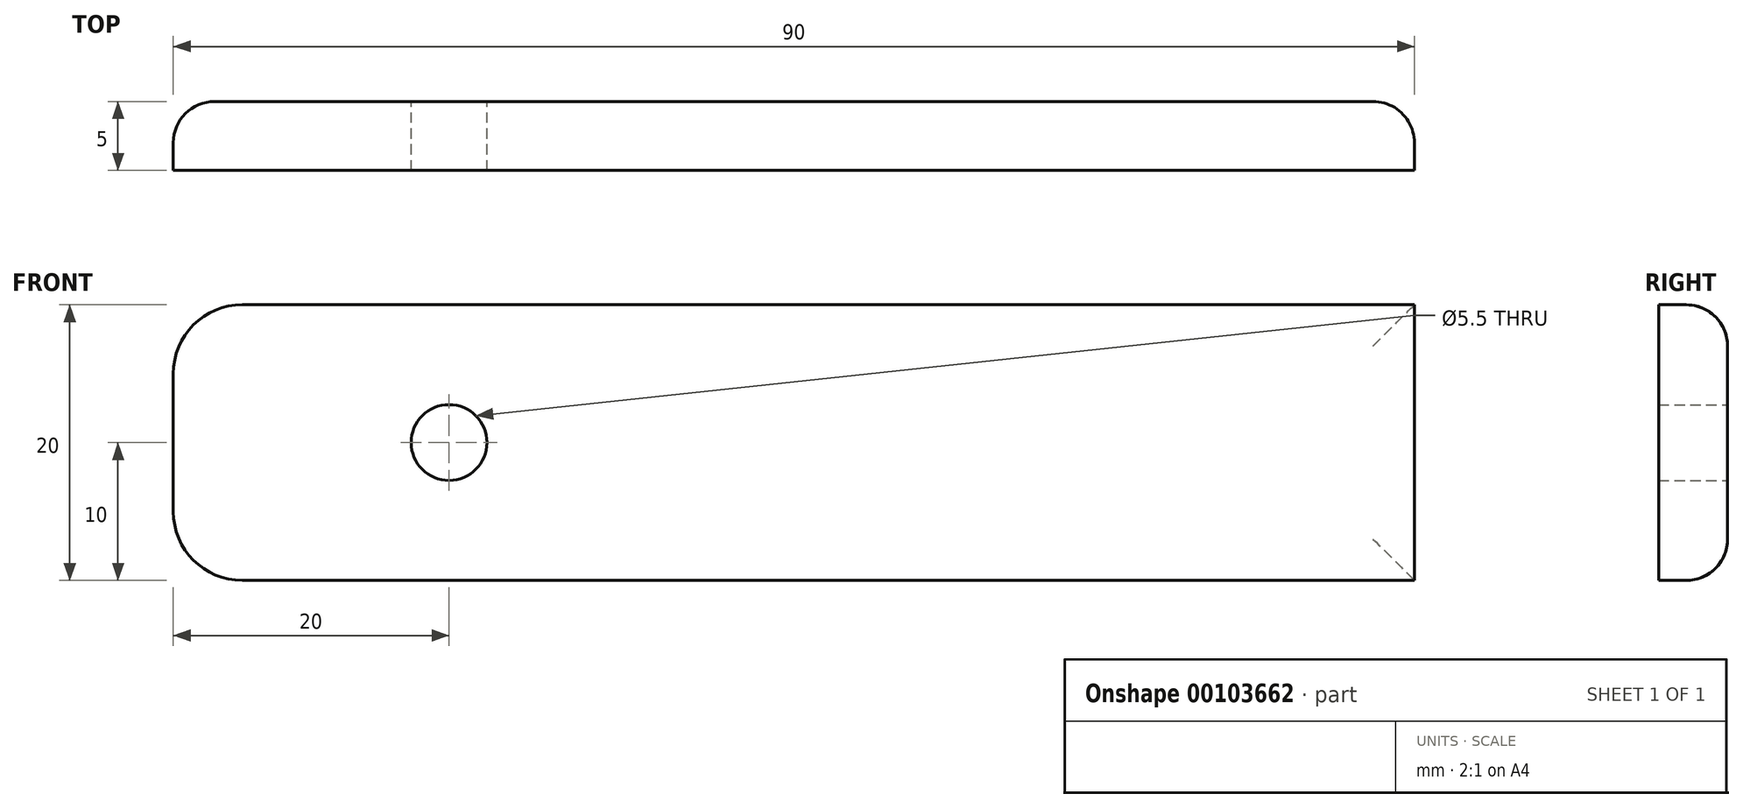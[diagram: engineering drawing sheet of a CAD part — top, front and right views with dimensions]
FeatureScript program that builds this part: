
annotation { "Feature Type Name" : "Feature", "Feature Type Description" : "" }
export const myFeature = defineFeature(function(context is Context, id is Id, definition is map)
    precondition{}
    {
        {
            var Q0;
            Q0=qCreatedBy(makeId("Top.planeOp"),FACE);
            var sketch = newSketch(context, id + "F0", { "sketchPlane" : qUnion([Q0])});
            skLineSegment(sketch, "E0.bottom", {"start": v(45, 2.5) * mm, "end": v(-45, 2.5) * mm});
            skLineSegment(sketch, "E0.top", {"start": v(45, -2.5) * mm, "end": v(-45, -2.5) * mm});
            skLineSegment(sketch, "E0.left", {"start": v(45, 2.5) * mm, "end": v(45, -2.5) * mm});
            skLineSegment(sketch, "E0.right", {"start": v(-45, 2.5) * mm, "end": v(-45, -2.5) * mm});
            skPoint(sketch, "E0.middle", {"position": v(0, 0) * mm});
            skLineSegment(sketch, "E1.left", {"start": v(45, -2.5) * mm, "end": v(45, 2.5) * mm});
            skLineSegment(sketch, "E2", {"start": v(45, -2.5) * mm, "end": v(59.13, 8.2) * mm});
            skLineSegment(sketch, "E3", {"start": v(45, 2.5) * mm, "end": v(56.96, 11.55) * mm});
            skLineSegment(sketch, "E4", {"start": v(56.96, 11.55) * mm, "end": v(59.13, 8.2) * mm});
            skSolve(sketch);
        }
        {
            var Q0;
            Q0=makeQuery(id+"F0.imprint","IMPRINT",FACE,{"disambiguationData":[TD([[makeQuery(id+"F0.imprint","IMPRINT",EDGE,{"derivedFrom":sQuery(id+"F0.wireOp",EDGE,"E0.bottom")}),1.0]])]});
            var Q1;
            Q1=makeQuery(id+"F0.imprint","IMPRINT",FACE,{"disambiguationData":[TD([[makeQuery(id+"F0.imprint","IMPRINT",EDGE,{"derivedFrom":sQuery(id+"F0.wireOp",EDGE,"E1.left")}),-1.0]])]});
            extrude(context, id + "F1", {"entities" : qUnion([Q0, Q1]), "depth" : 20 * mm});
        }
        {
            var Q0;
            Q0=makeQuery(id+"F1.opExtrude","SWEPT_FACE",FACE,{"disambiguationData":[OSD([sQuery(id+"F0.wireOp",EDGE,"E0.bottom")])]});
            var sketch = newSketch(context, id + "F2", { "sketchPlane" : qUnion([Q0])});
            skLineSegment(sketch, "E5", {"start": v(45, 10) * mm, "end": v(-45, 10) * mm, "construction": true});
            skCircle(sketch, "E6", {"center": v(25, 10) * mm, "radius": 2.75 * mm});
            skSolve(sketch);
        }
        {
            var Q0;
            Q0=makeQuery(id+"F2.imprint","IMPRINT",FACE,{"disambiguationData":[TD([[makeQuery(id+"F2.imprint","IMPRINT",EDGE,{"derivedFrom":sQuery(id+"F2.wireOp",EDGE,"E6")}),1.0]])]});
            var Q1;
            Q1=makeQuery(id+"F1.opExtrude","SWEPT_FACE",FACE,{"disambiguationData":[OSD([sQuery(id+"F0.wireOp",EDGE,"E0.top")])]});
            extrude(context, id + "F3", {"entities" : qUnion([Q0]), "operationType" : NewBodyOperationType.REMOVE, "endBound" : BoundingType.UP_TO_SURFACE, "oppositeDirection" : true, "endBoundEntityFace" : qUnion([Q1]), "depth" : 25 * mm});
        }
        {
            var Q0;
            Q0=makeQuery(id+"F1.opExtrude","CAP_EDGE",EDGE,{"disambiguationData":[OSD([sQuery(id+"F0.wireOp",EDGE,"E4")])],"isStart":false});
            var Q1;
            Q1=makeQuery(id+"F1.opExtrude","CAP_EDGE",EDGE,{"disambiguationData":[OSD([sQuery(id+"F0.wireOp",EDGE,"E4")])],"isStart":true});
            var Q2;
            Q2=makeQuery(id+"F1.opExtrude","CAP_EDGE",EDGE,{"disambiguationData":[OSD([sQuery(id+"F0.wireOp",EDGE,"E0.right")])],"isStart":false});
            var Q3;
            Q3=makeQuery(id+"F1.opExtrude","CAP_EDGE",EDGE,{"disambiguationData":[OSD([sQuery(id+"F0.wireOp",EDGE,"E0.right")])],"isStart":true});
            fillet(context, id + "F4", {"entities" : qUnion([Q0, Q1, Q2, Q3]), "radius" : 5 * mm, "tangentPropagation" : true, "allowEdgeOverflow" : false});
        }
        {
            var Q0;
            Q0=makeQuery(id+"F1.opExtrude","CAP_EDGE",EDGE,{"disambiguationData":[OSD([sQuery(id+"F0.wireOp",EDGE,"E0.bottom")])],"isStart":false});
            var Q1;
            Q1=makeQuery(id+"F4.opFillet","BLEND_EDGE",EDGE,{"blendedFrom":[makeQuery(id+"F1.opExtrude","CAP_EDGE",EDGE,{"disambiguationData":[OSD([sQuery(id+"F0.wireOp",EDGE,"E0.right")])],"isStart":false}),makeQuery(id+"F1.opExtrude","SWEPT_FACE",FACE,{"disambiguationData":[OSD([sQuery(id+"F0.wireOp",EDGE,"E0.bottom")])]})],"blendedInto":[makeQuery(id+"F1.opExtrude","SWEPT_FACE",FACE,{"disambiguationData":[OSD([sQuery(id+"F0.wireOp",EDGE,"E0.bottom")])]})]});
            var Q2;
            Q2=makeQuery(id+"F1.opExtrude","SWEPT_EDGE",EDGE,{"disambiguationData":[OSD([sQuery(id+"F0.wireOp",EDGE,"E0.bottom"),sQuery(id+"F0.wireOp",EDGE,"E0.right")])]});
            var Q3;
            Q3=makeQuery(id+"F4.opFillet","BLEND_EDGE",EDGE,{"blendedFrom":[makeQuery(id+"F1.opExtrude","CAP_EDGE",EDGE,{"disambiguationData":[OSD([sQuery(id+"F0.wireOp",EDGE,"E0.right")])],"isStart":true}),makeQuery(id+"F1.opExtrude","SWEPT_FACE",FACE,{"disambiguationData":[OSD([sQuery(id+"F0.wireOp",EDGE,"E0.bottom")])]})],"blendedInto":[makeQuery(id+"F1.opExtrude","SWEPT_FACE",FACE,{"disambiguationData":[OSD([sQuery(id+"F0.wireOp",EDGE,"E0.bottom")])]})]});
            var Q4;
            Q4=makeQuery(id+"F1.opExtrude","CAP_EDGE",EDGE,{"disambiguationData":[OSD([sQuery(id+"F0.wireOp",EDGE,"E0.bottom")])],"isStart":true});
            var Q5;
            Q5=makeQuery(id+"F1.opExtrude","SWEPT_EDGE",EDGE,{"disambiguationData":[OSD([sQuery(id+"F0.wireOp",EDGE,"E3"),sQuery(id+"F0.wireOp",EDGE,"E4")])]});
            var Q6;
            Q6=makeQuery(id+"F4.opFillet","BLEND_EDGE",EDGE,{"blendedFrom":[makeQuery(id+"F1.opExtrude","CAP_EDGE",EDGE,{"disambiguationData":[OSD([sQuery(id+"F0.wireOp",EDGE,"E4")])],"isStart":true}),makeQuery(id+"F1.opExtrude","SWEPT_FACE",FACE,{"disambiguationData":[OSD([sQuery(id+"F0.wireOp",EDGE,"E3")])]})],"blendedInto":[makeQuery(id+"F1.opExtrude","SWEPT_FACE",FACE,{"disambiguationData":[OSD([sQuery(id+"F0.wireOp",EDGE,"E3")])]})]});
            var Q7;
            Q7=makeQuery(id+"F1.opExtrude","CAP_EDGE",EDGE,{"disambiguationData":[OSD([sQuery(id+"F0.wireOp",EDGE,"E3")])],"isStart":true});
            var Q8;
            Q8=makeQuery(id+"F4.opFillet","BLEND_EDGE",EDGE,{"blendedFrom":[makeQuery(id+"F1.opExtrude","CAP_EDGE",EDGE,{"disambiguationData":[OSD([sQuery(id+"F0.wireOp",EDGE,"E4")])],"isStart":false}),makeQuery(id+"F1.opExtrude","SWEPT_FACE",FACE,{"disambiguationData":[OSD([sQuery(id+"F0.wireOp",EDGE,"E3")])]})],"blendedInto":[makeQuery(id+"F1.opExtrude","SWEPT_FACE",FACE,{"disambiguationData":[OSD([sQuery(id+"F0.wireOp",EDGE,"E3")])]})]});
            var Q9;
            Q9=makeQuery(id+"F1.opExtrude","CAP_EDGE",EDGE,{"disambiguationData":[OSD([sQuery(id+"F0.wireOp",EDGE,"E3")])],"isStart":false});
            fillet(context, id + "F5", {"entities" : qUnion([Q0, Q1, Q2, Q3, Q4, Q5, Q6, Q7, Q8, Q9]), "radius" : 3 * mm, "tangentPropagation" : true, "allowEdgeOverflow" : false});
        }
    });
